# Revit family: DE_MEADRAIN_DM_Basic
name_source: partatom
category: Allgemeines Modell
revit_build: Autodesk Revit 2018 (Build: 20170223_1515(x64)
units: mm (PartAtom-declared; Revit-internal decimal feet)

## family parameters
Beim Laden mit Abzugskörper schneiden = Ja
Bemaßung runder Anschluss = Durchmesser verwenden
Gemeinsam genutzt = Nein
Kann Basisbauteil für Bewehrung sein = Nein
Raumberechnungspunkt = Nein
Teiletyp = Normal

## types (17) — shared parameters
Abdeckung = Gussrost
Außendurchmesser_Ablaufstutzen_Einlaufkasten = 122 mm  [stored 0.400262 ft]
Außendurchmesser_Ablaufstutzen_Sinkasten = 160 mm  [stored 0.524934 ft]
B_Innendurchmesser_Ablaufstutzen_Sinkasten = 150 mm  [stored 0.492126 ft]
Bauelement = Entwässerungsrinne Oberflächenwasser
Baustoff, Bettung/Fundament = gemäß Zeichnung und Einzelbeschreibung
Bauteil,Entwässerung = Entwässerungsrinne
Beschreibung = Universal Entwässerungssystem aus Polymerbeton
Eigung Entwässerungsbauteil = Für besondere Ansprüche im Bereich vpn Schnellstraßen und Autobahnen ist das System MEADRAIN DM bestebs geeignet. Verschiedene Nennweiten für die unterschiedlichen Anforderungen.
Einbautechnologie = Typ M
Gefälleart-/-Prozente Enwässerungsbauteil = Ohne Gefälle
Hersteller = MEA Bautechnik GmbH Geschäftsbereich MEA Water  Management
Hersteller und Typ- Ausschreibender gleichwertig = wie MEA Bautechnik GmbH, Modell MEADRAIN DM
IfcDescription = Universal Entwässerungssystem aus Polymerbeton
IfcExportAs = IfcWasteTerminalType
IfcExportType = USERDEFINED
MEA Plannungshilfe = einschl. Fundament und Ummantelung
Modell = MEADRAIN DM
Produktwebsite = https://www.mea-group.com
Stirnplatte_Dicke = 3 mm  [stored 0.00984252 ft]
Technische Produktinformation = https://www.mea-group.com
Typ Entwässerungsbauteil = Beton
Typenkommentare = Für besondere Ansprüche im Bereich vpn Schnellstraßen und Autobahnen ist das System MEADRAIN DM bestebs geeignet. Verschiedene Nennweiten für die unterschiedlichen Anforderungen.
guid = cf6c1bd8-9bf4-4563-8c57-07955e2378ac

## per-type parameters (varying)
| type | ArtikelnummerAbdeckung 1 | ArtikelnummerAbdeckung 2 | Artikelnummer_Rinne | Artikelnummer_SKOT | Artikelnummer_Stirnplatte | Ausführungsunterlagen | Außendurchmesser_Ablaufstutzen_Revisionselement | B_Breite | B_H01 | B_Höhe_Einlaufkasten | B_Innendurchmesser_Ablaufstutzen | Belastungsklasse Entwässerungsbauteil | Breite_Rinnen | Def Belastungsklasse_Rinne | Einlaufkasten_Artikelnummer | Fundament_Breite | Höhe | Länge_Ablaufstutzen_Einlaufkasten | Länge_Ablaufstutzen_Revisionselement | MEA-Belastungsklasse | MEA-Nennweite mm | Nennweite | Revision_Ablaufstutzen_Artikelnummer | Revision_Artikelnummer |
| DM 1010 | - | 010153094 | 010712884 |  | 010712900 |  | 22 mm  [stored 0.0721785 ft] | 154 mm  [stored 0.505249 ft] | 265 mm  [stored 0.869423 ft] | 580 mm  [stored 1.90289 ft] | 2 mm  [stored 0.00656168 ft] | F900 | 154 mm  [stored 0.505249 ft] | F900 | 010712898 | 250 mm  [stored 0.82021 ft] | 265 mm  [stored 0.869423 ft] | 30 mm  [stored 0.0984252 ft] | 130 mm  [stored 0.426509 ft] | F900 | 1010 | 100 mm  [stored 0.328084 ft] | - | 010712896 |
| DM 1500 | 010151173 | 010151169 | 010712938 | 010712952 | 010712954 |  | 22 mm  [stored 0.0721785 ft] | 204 mm  [stored 0.669291 ft] | 280 mm  [stored 0.918635 ft] | 860 mm | 2 mm  [stored 0.00656168 ft] | F900 | 204 mm  [stored 0.669291 ft] | F900 |  | 250 mm  [stored 0.82021 ft] | 280 mm  [stored 0.918635 ft] | 194 mm  [stored 0.636483 ft] | 130 mm  [stored 0.426509 ft] | F900 | 1500 | 150 mm  [stored 0.492126 ft] | - | 010712950 |
| DM 1540 | 010151173 | 010151169 | 010712902 | 010712916 | 010712918 |  | 160 mm  [stored 0.524934 ft] | 204 mm  [stored 0.669291 ft] | 480 mm  [stored 1.5748 ft] | 860 mm | 140 mm  [stored 0.459318 ft] | F900 | 204 mm  [stored 0.669291 ft] | F900 |  | 250 mm  [stored 0.82021 ft] | 480 mm  [stored 1.5748 ft] | 194 mm  [stored 0.636483 ft] | 130 mm  [stored 0.426509 ft] | F900 | 1540 | 150 mm  [stored 0.492126 ft] | 010712384 | 010712383 |
| DM 2000 | 010154236 | 010154237 | 010712357 | 010712369 | 010712375 |  | 200 mm  [stored 0.656168 ft] | 254 mm  [stored 0.833333 ft] | 320 mm  [stored 1.04987 ft] | 700 mm  [stored 2.29659 ft] | 180 mm  [stored 0.590551 ft] | F900 | 254 mm  [stored 0.833333 ft] | F900 |  | 250 mm  [stored 0.82021 ft] | 320 mm  [stored 1.04987 ft] | 194 mm  [stored 0.636483 ft] | 180 mm  [stored 0.590551 ft] | F900 | 2000 | 200 mm  [stored 0.656168 ft] | 010714908 | 010712386 |
| DM 2020 | 010154236 | 010154237 | 010712804 | 010712816 | 010712822 |  | 200 mm  [stored 0.656168 ft] | 254 mm  [stored 0.833333 ft] | 420 mm  [stored 1.37795 ft] | 800 mm  [stored 2.62467 ft] | 180 mm  [stored 0.590551 ft] | E600 | 254 mm  [stored 0.833333 ft] | E600 |  | 200 mm  [stored 0.656168 ft] | 420 mm  [stored 1.37795 ft] | 194 mm  [stored 0.636483 ft] | 180 mm  [stored 0.590551 ft] | E600 | 2020 | 200 mm  [stored 0.656168 ft] | 010714910 | 010712385 |
| DM 2040 | 010154236 | 010154237 | 010712782 | 010712798 | 010712800 | https://www.mea-group.com | 200 mm  [stored 0.656168 ft] | 254 mm  [stored 0.833333 ft] | 520 mm  [stored 1.70604 ft] | 950 mm  [stored 3.1168 ft] | 180 mm  [stored 0.590551 ft] | E600 | 254 mm  [stored 0.833333 ft] | E600 |  | 200 mm  [stored 0.656168 ft] | 520 mm  [stored 1.70604 ft] | 194 mm  [stored 0.636483 ft] | 180 mm  [stored 0.590551 ft] | E600 | 2040 | 200 mm  [stored 0.656168 ft] | 010714912 | 010712389 |
| DM 2050 | 010154236 | 010154237 | 010712762 | 010712778 | 010712780 |  | 200 mm  [stored 0.656168 ft] | 254 mm  [stored 0.833333 ft] | 559 mm  [stored 1.83399 ft] | 950 mm  [stored 3.1168 ft] | 180 mm  [stored 0.590551 ft] | E600 | 254 mm  [stored 0.833333 ft] | E600 |  | 200 mm  [stored 0.656168 ft] | 559 mm  [stored 1.83399 ft] | 194 mm  [stored 0.636483 ft] | 180 mm  [stored 0.590551 ft] | E600 | 2050 | 200 mm  [stored 0.656168 ft] | 010714914 | 010712390 |
| DM 1500 DAR | 010151173 | 010151169 | 010712956 | 010712952 | 010712954 |  | 22 mm  [stored 0.0721785 ft] | 204 mm  [stored 0.669291 ft] | 280 mm  [stored 0.918635 ft] | 860 mm | 2 mm  [stored 0.00656168 ft] | F900 | 204 mm  [stored 0.669291 ft] | F900 |  | 250 mm  [stored 0.82021 ft] | 280 mm  [stored 0.918635 ft] | 194 mm  [stored 0.636483 ft] | 130 mm  [stored 0.426509 ft] | F900 | 1500 DAR | 150 mm  [stored 0.492126 ft] | - | 010712950 |
| DM 1500 DAL | 010151173 | 010151169 | 010712938 | 010712952 | 010712954 |  | 22 mm  [stored 0.0721785 ft] | 204 mm  [stored 0.669291 ft] | 280 mm  [stored 0.918635 ft] | 860 mm | 2 mm  [stored 0.00656168 ft] | F900 | 204 mm  [stored 0.669291 ft] | F900 |  | 250 mm  [stored 0.82021 ft] | 280 mm  [stored 0.918635 ft] | 194 mm  [stored 0.636483 ft] | 130 mm  [stored 0.426509 ft] | F900 | 1500 DAL | 150 mm  [stored 0.492126 ft] | - | 010712950 |
| DM 1540 DAR | 010151173 | 010151169 | 010712910 | 010712916 | 010712918 |  | 160 mm  [stored 0.524934 ft] | 204 mm  [stored 0.669291 ft] | 480 mm  [stored 1.5748 ft] | 860 mm | 140 mm  [stored 0.459318 ft] | F900 | 204 mm  [stored 0.669291 ft] | F900 |  | 250 mm  [stored 0.82021 ft] | 480 mm  [stored 1.5748 ft] | 194 mm  [stored 0.636483 ft] | 130 mm  [stored 0.426509 ft] | F900 | 1540 DAR | 150 mm  [stored 0.492126 ft] | 010712384 | 010712383 |
| DM 1540 DAL | 010151173 | 010151169 | 010712906 | 010712916 | 010712918 |  | 160 mm  [stored 0.524934 ft] | 204 mm  [stored 0.669291 ft] | 480 mm  [stored 1.5748 ft] | 860 mm | 140 mm  [stored 0.459318 ft] | F900 | 204 mm  [stored 0.669291 ft] | F900 |  | 250 mm  [stored 0.82021 ft] | 480 mm  [stored 1.5748 ft] | 194 mm  [stored 0.636483 ft] | 130 mm  [stored 0.426509 ft] | F900 | 1540 DAL | 150 mm  [stored 0.492126 ft] | 010712384 | 010712383 |
| DM 2000 DAR | 010154236 | 010154237 | 010712393 | 010712369 | 010712375 |  | 200 mm  [stored 0.656168 ft] | 254 mm  [stored 0.833333 ft] | 320 mm  [stored 1.04987 ft] | 700 mm  [stored 2.29659 ft] | 180 mm  [stored 0.590551 ft] | F900 | 254 mm  [stored 0.833333 ft] | F900 |  | 250 mm  [stored 0.82021 ft] | 320 mm  [stored 1.04987 ft] | 194 mm  [stored 0.636483 ft] | 180 mm  [stored 0.590551 ft] | F900 | 2000 DAR | 200 mm  [stored 0.656168 ft] | 010714908 | 010712386 |
| DM 2000 DAL | 010154236 | 010154237 | 010712387 | 010712369 | 010712375 |  | 200 mm  [stored 0.656168 ft] | 254 mm  [stored 0.833333 ft] | 320 mm  [stored 1.04987 ft] | 700 mm  [stored 2.29659 ft] | 180 mm  [stored 0.590551 ft] | F900 | 254 mm  [stored 0.833333 ft] | F900 |  | 250 mm  [stored 0.82021 ft] | 320 mm  [stored 1.04987 ft] | 194 mm  [stored 0.636483 ft] | 180 mm  [stored 0.590551 ft] | F900 | 2000 DAL | 200 mm  [stored 0.656168 ft] | 010714908 | 010712386 |
| DM 2020 DAR | 010154236 | 010154237 | 010712812 | 010712816 | 010712822 |  | 200 mm  [stored 0.656168 ft] | 254 mm  [stored 0.833333 ft] | 420 mm  [stored 1.37795 ft] | 800 mm  [stored 2.62467 ft] | 180 mm  [stored 0.590551 ft] | E600 | 254 mm  [stored 0.833333 ft] | E600 |  | 200 mm  [stored 0.656168 ft] | 420 mm  [stored 1.37795 ft] | 194 mm  [stored 0.636483 ft] | 180 mm  [stored 0.590551 ft] | E600 | 2020 DAR | 200 mm  [stored 0.656168 ft] | 010714910 | 010712385 |
| DM 2020 DAL | 010154236 | 010154237 | 010712808 | 010712816 | 010712822 |  | 200 mm  [stored 0.656168 ft] | 254 mm  [stored 0.833333 ft] | 420 mm  [stored 1.37795 ft] | 800 mm  [stored 2.62467 ft] | 180 mm  [stored 0.590551 ft] | E600 | 254 mm  [stored 0.833333 ft] | E600 |  | 200 mm  [stored 0.656168 ft] | 420 mm  [stored 1.37795 ft] | 194 mm  [stored 0.636483 ft] | 180 mm  [stored 0.590551 ft] | E600 | 2020 DAL | 200 mm  [stored 0.656168 ft] | 010714910 | 010712385 |
| DM 2040 DAR | 010154236 | 010154237 | 010712924 | 010712798 | 010712800 |  | 200 mm  [stored 0.656168 ft] | 254 mm  [stored 0.833333 ft] | 520 mm  [stored 1.70604 ft] | 950 mm  [stored 3.1168 ft] | 180 mm  [stored 0.590551 ft] | E600 | 254 mm  [stored 0.833333 ft] | E600 |  | 200 mm  [stored 0.656168 ft] | 520 mm  [stored 1.70604 ft] | 194 mm  [stored 0.636483 ft] | 180 mm  [stored 0.590551 ft] | E600 | 2040 DAR | 200 mm  [stored 0.656168 ft] | 010714912 | 010712389 |
| DM 2040 DAL | 010154236 | 010154237 | 010712920 | 010712798 | 010712800 |  | 200 mm  [stored 0.656168 ft] | 254 mm  [stored 0.833333 ft] | 520 mm  [stored 1.70604 ft] | 950 mm  [stored 3.1168 ft] | 180 mm  [stored 0.590551 ft] | E600 | 254 mm  [stored 0.833333 ft] | E600 |  | 200 mm  [stored 0.656168 ft] | 520 mm  [stored 1.70604 ft] | 194 mm  [stored 0.636483 ft] | 180 mm  [stored 0.590551 ft] | E600 | 2040 DAL | 200 mm  [stored 0.656168 ft] | 010714912 | 010712389 |

note: [stored X ft] marks values corroborated as IEEE doubles in the binary element streams (Revit-internal decimal feet)
